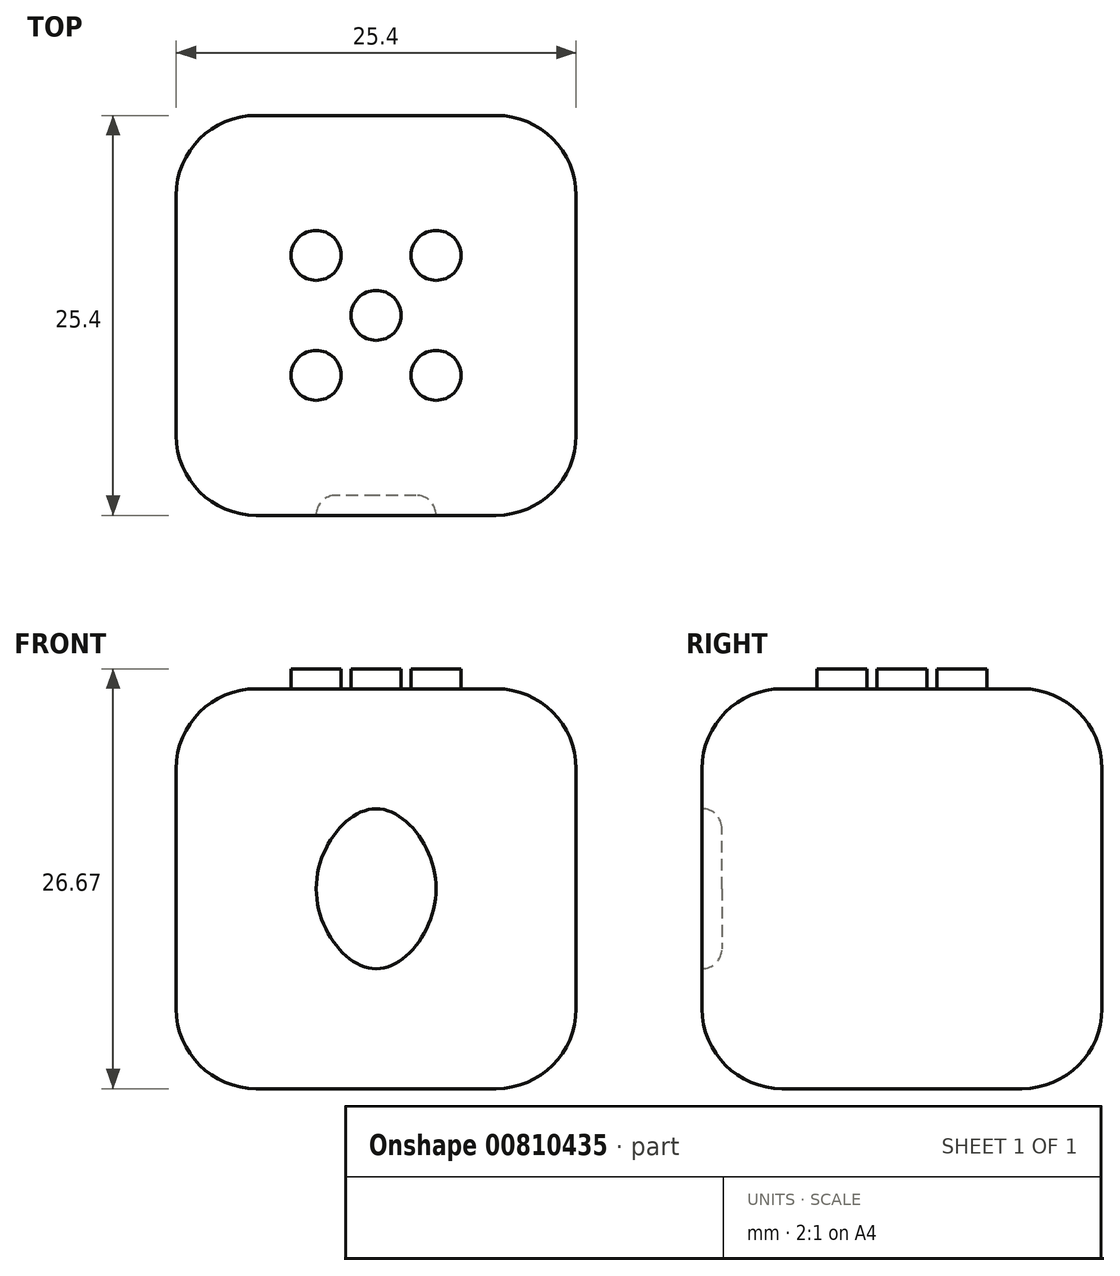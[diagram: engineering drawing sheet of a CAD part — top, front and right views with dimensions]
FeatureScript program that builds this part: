
annotation { "Feature Type Name" : "Feature", "Feature Type Description" : "" }
export const myFeature = defineFeature(function(context is Context, id is Id, definition is map)
    precondition{}
    {
        {
            var Q0;
            Q0=qCreatedBy(makeId("Top.planeOp"),FACE);
            var sketch = newSketch(context, id + "F0", { "sketchPlane" : qUnion([Q0])});
            skLineSegment(sketch, "E0.bottom", {"start": v(12.7, 12.7) * mm, "end": v(-12.7, 12.7) * mm});
            skLineSegment(sketch, "E0.top", {"start": v(12.7, -12.7) * mm, "end": v(-12.7, -12.7) * mm});
            skLineSegment(sketch, "E0.left", {"start": v(12.7, 12.7) * mm, "end": v(12.7, -12.7) * mm});
            skLineSegment(sketch, "E0.right", {"start": v(-12.7, 12.7) * mm, "end": v(-12.7, -12.7) * mm});
            skPoint(sketch, "E0.middle", {"position": v(0, 0) * mm});
            skSolve(sketch);
        }
        {
            var Q0;
            Q0=makeQuery(id+"F0.imprint","IMPRINT",FACE,{"disambiguationData":[TD([[makeQuery(id+"F0.imprint","IMPRINT",EDGE,{"derivedFrom":sQuery(id+"F0.wireOp",EDGE,"E0.bottom")}),1.0]])]});
            extrude(context, id + "F1", {"entities" : qUnion([Q0]), "endBound" : BoundingType.SYMMETRIC, "depth" : 25.4 * mm, "offsetDistance" : 25.4 * mm});
        }
        {
            var Q0;
            Q0=makeQuery(id+"F1.opExtrude","CAP_EDGE",EDGE,{"disambiguationData":[OSD([sQuery(id+"F0.wireOp",EDGE,"E0.left")])],"isStart":false});
            var Q1;
            Q1=makeQuery(id+"F1.opExtrude","CAP_EDGE",EDGE,{"disambiguationData":[OSD([sQuery(id+"F0.wireOp",EDGE,"E0.bottom")])],"isStart":false});
            var Q2;
            Q2=makeQuery(id+"F1.opExtrude","CAP_EDGE",EDGE,{"disambiguationData":[OSD([sQuery(id+"F0.wireOp",EDGE,"E0.right")])],"isStart":false});
            var Q3;
            Q3=makeQuery(id+"F1.opExtrude","CAP_EDGE",EDGE,{"disambiguationData":[OSD([sQuery(id+"F0.wireOp",EDGE,"E0.top")])],"isStart":false});
            var Q4;
            Q4=makeQuery(id+"F1.opExtrude","SWEPT_FACE",FACE,{"disambiguationData":[OSD([sQuery(id+"F0.wireOp",EDGE,"E0.left")])]});
            var Q5;
            Q5=makeQuery(id+"F1.opExtrude","SWEPT_EDGE",EDGE,{"disambiguationData":[OSD([sQuery(id+"F0.wireOp",EDGE,"E0.bottom"),sQuery(id+"F0.wireOp",EDGE,"E0.right")])]});
            var Q6;
            Q6=makeQuery(id+"F1.opExtrude","SWEPT_EDGE",EDGE,{"disambiguationData":[OSD([sQuery(id+"F0.wireOp",EDGE,"E0.top"),sQuery(id+"F0.wireOp",EDGE,"E0.right")])]});
            var Q7;
            Q7=makeQuery(id+"F1.opExtrude","CAP_EDGE",EDGE,{"disambiguationData":[OSD([sQuery(id+"F0.wireOp",EDGE,"E0.top")])],"isStart":true});
            var Q8;
            Q8=makeQuery(id+"F1.opExtrude","CAP_EDGE",EDGE,{"disambiguationData":[OSD([sQuery(id+"F0.wireOp",EDGE,"E0.right")])],"isStart":true});
            var Q9;
            Q9=makeQuery(id+"F1.opExtrude","CAP_EDGE",EDGE,{"disambiguationData":[OSD([sQuery(id+"F0.wireOp",EDGE,"E0.bottom")])],"isStart":true});
            fillet(context, id + "F2", {"entities" : qUnion([Q0, Q1, Q2, Q3, Q4, Q5, Q6, Q7, Q8, Q9]), "radius" : 5.08 * mm, "tangentPropagation" : true, "allowEdgeOverflow" : false});
        }
        {
            var Q0;
            Q0=makeQuery(id+"F1.opExtrude","SWEPT_FACE",FACE,{"disambiguationData":[OSD([sQuery(id+"F0.wireOp",EDGE,"E0.top")])]});
            var sketch = newSketch(context, id + "F3", { "sketchPlane" : qUnion([Q0])});
            skFitSpline(sketch, "E1", {"points": [v(0, 5.08) * mm, v(3.81, 0) * mm, v(0, -5.08) * mm, v(-3.81, 0) * mm, v(0, 5.08) * mm]});
            skLineSegment(sketch, "E2", {"start": v(-3.81, 0) * mm, "end": v(0, 0) * mm});
            skLineSegment(sketch, "E3", {"start": v(0, 5.08) * mm, "end": v(0, 0) * mm});
            skLineSegment(sketch, "E4", {"start": v(0, 0) * mm, "end": v(3.81, 0) * mm});
            skLineSegment(sketch, "E5", {"start": v(0, 0) * mm, "end": v(0, -5.08) * mm});
            skPoint(sketch, "E6", {"position": v(0, 12.7) * mm});
            skSolve(sketch);
        }
        {
            var Q0;
            Q0 = qSketchRegion(id + "F3", true);
            extrude(context, id + "F4", {"entities" : qUnion([Q0]), "operationType" : NewBodyOperationType.REMOVE, "oppositeDirection" : true, "depth" : 1.27 * mm, "offsetDistance" : 25.4 * mm});
        }
        {
            var Q0;
            Q0=makeQuery(id+"F4.boolean.opBoolean","COPY",EDGE,{"derivedFrom":makeQuery(id+"F4.opExtrude","CAP_EDGE",EDGE,{"disambiguationData":[OSD([sQuery(id+"F3.wireOp",EDGE,"E1")])],"isStart":false})});
            fillet(context, id + "F5", {"entities" : qUnion([Q0]), "radius" : 1.27 * mm, "tangentPropagation" : true, "allowEdgeOverflow" : false});
        }
        {
            var Q0;
            Q0=makeQuery(id+"F1.opExtrude","CAP_FACE",FACE,{"disambiguationData":[OSD([sQuery(id+"F0.wireOp",EDGE,"E0.bottom"),sQuery(id+"F0.wireOp",EDGE,"E0.top"),sQuery(id+"F0.wireOp",EDGE,"E0.left"),sQuery(id+"F0.wireOp",EDGE,"E0.right")])],"isStart":false});
            var sketch = newSketch(context, id + "F6", { "sketchPlane" : qUnion([Q0])});
            skCircle(sketch, "E7", {"center": v(0, 0) * mm, "radius": 1.59 * mm});
            skLineSegment(sketch, "E8", {"start": v(7.62, 7.62) * mm, "end": v(-7.62, -7.62) * mm, "construction": true});
            skLineSegment(sketch, "E9", {"start": v(-7.62, 7.62) * mm, "end": v(7.62, -7.62) * mm, "construction": true});
            skLineSegment(sketch, "E10", {"start": v(0, -7.62) * mm, "end": v(7.62, 0) * mm, "construction": true});
            skLineSegment(sketch, "E11", {"start": v(7.62, 0) * mm, "end": v(0, 7.62) * mm, "construction": true});
            skLineSegment(sketch, "E12", {"start": v(0, 7.62) * mm, "end": v(-7.62, 0) * mm, "construction": true});
            skLineSegment(sketch, "E13", {"start": v(-7.62, 0) * mm, "end": v(0, -7.62) * mm, "construction": true});
            skCircle(sketch, "E14", {"center": v(-3.81, 3.81) * mm, "radius": 1.59 * mm});
            skCircle(sketch, "E15", {"center": v(-3.81, -3.81) * mm, "radius": 1.59 * mm});
            skCircle(sketch, "E16", {"center": v(3.81, -3.81) * mm, "radius": 1.59 * mm});
            skCircle(sketch, "E17", {"center": v(3.81, 3.81) * mm, "radius": 1.59 * mm});
            skSolve(sketch);
        }
        {
            var Q0;
            Q0 = qSketchRegion(id + "F6", true);
            extrude(context, id + "F7", {"entities" : qUnion([Q0]), "operationType" : NewBodyOperationType.ADD, "depth" : 1.27 * mm, "offsetDistance" : 25.4 * mm});
        }
    });
